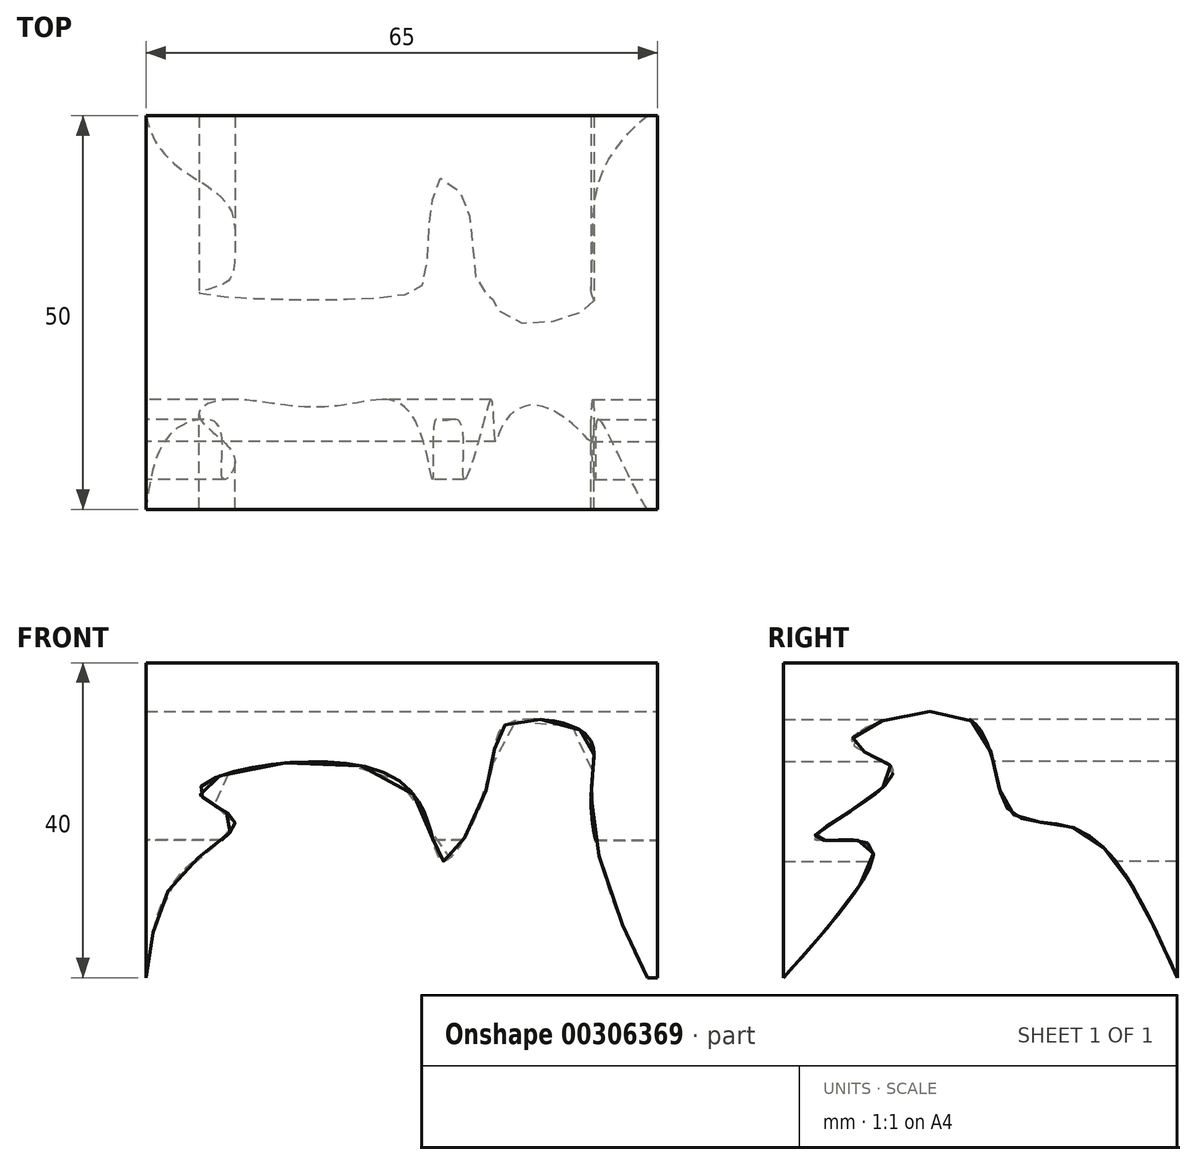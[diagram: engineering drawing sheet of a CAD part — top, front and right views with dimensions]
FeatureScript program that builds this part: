
annotation { "Feature Type Name" : "Feature", "Feature Type Description" : "" }
export const myFeature = defineFeature(function(context is Context, id is Id, definition is map)
    precondition{}
    {
        {
            var Q0;
            Q0=qCreatedBy(makeId("Front.planeOp"),FACE);
            var sketch = newSketch(context, id + "F0", { "sketchPlane" : qUnion([Q0])});
            skLineSegment(sketch, "E0.bottom", {"start": v(0, 0) * mm, "end": v(65, 0) * mm});
            skLineSegment(sketch, "E0.top", {"start": v(0, 40) * mm, "end": v(65, 40) * mm});
            skLineSegment(sketch, "E0.left", {"start": v(0, 0) * mm, "end": v(0, 40) * mm});
            skLineSegment(sketch, "E0.right", {"start": v(65, 0) * mm, "end": v(65, 40) * mm});
            skPoint(sketch, "E1.2.internal.snap0", {"position": v(0, 20) * mm});
            skPoint(sketch, "E1.9.internal.snap0", {"position": v(0, 20) * mm});
            skFitSpline(sketch, "E1", {"points": [v(0, 0) * mm, v(4.62, 13.48) * mm, v(11.23, 20) * mm, v(6.74, 23.78) * mm, v(32.1, 25.1) * mm, v(37.66, 14.8) * mm, v(43.74, 25.63) * mm, v(45.85, 32.24) * mm, v(55.9, 30.92) * mm, v(56.68, 20) * mm, v(65, -1.85) * mm, v(65, 0) * mm], "startDerivative": vector(17.4, 144) * mm, "endDerivative": vector(-11.45, 77.48) * mm});
            skSolve(sketch);
        }
        {
            var Q0;
            Q0=makeQuery(id+"F0.imprint","IMPRINT",FACE,{"disambiguationData":[TD([[makeQuery(id+"F0.imprint","IMPRINT",EDGE,{"derivedFrom":sQuery(id+"F0.wireOp",EDGE,"E0.top")}),-1.0]])]});
            extrude(context, id + "F1", {"entities" : qUnion([Q0]), "depth" : 50 * mm});
        }
        {
            var Q0;
            Q0=makeQuery(id+"F1.opExtrude","SWEPT_FACE",FACE,{"disambiguationData":[OSD([sQuery(id+"F0.wireOp",EDGE,"E0.right")])]});
            var sketch = newSketch(context, id + "F2", { "sketchPlane" : qUnion([Q0])});
            skFitSpline(sketch, "E2", {"points": [v(-50, 0) * mm, v(-39.3, 17.13) * mm, v(-46.21, 17.76) * mm, v(-36.04, 26.18) * mm, v(-41.35, 29.9) * mm, v(-26.86, 33.08) * mm, v(-21.43, 21.33) * mm, v(-12.53, 18.8) * mm, v(0, 0) * mm], "startDerivative": vector(131.01, 147.57) * mm, "endDerivative": vector(66.7, -149.44) * mm});
            skSolve(sketch);
        }
        {
            var Q0;
            Q0=makeQuery(id+"F2.imprint","IMPRINT",FACE,{"disambiguationData":[TD([[makeQuery(id+"F2.imprint","IMPRINT",EDGE,{"derivedFrom":sQuery(id+"F2.wireOp",EDGE,"E2")}),-1.0]])]});
            extrude(context, id + "F3", {"entities" : qUnion([Q0]), "operationType" : NewBodyOperationType.REMOVE, "endBound" : BoundingType.THROUGH_ALL, "oppositeDirection" : true, "depth" : 25 * mm});
        }
    });
